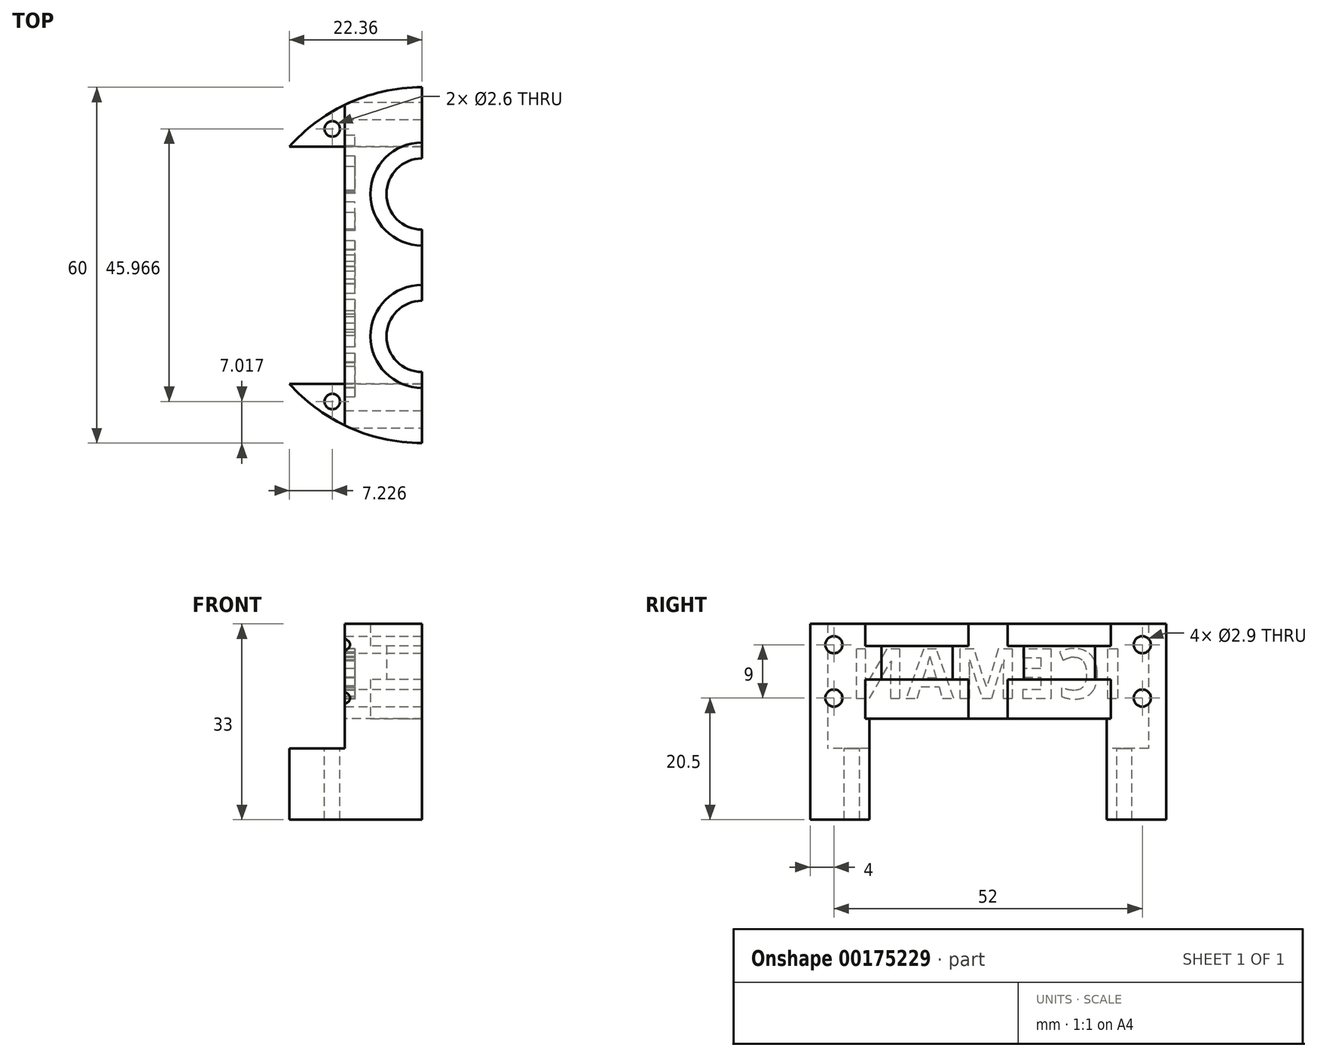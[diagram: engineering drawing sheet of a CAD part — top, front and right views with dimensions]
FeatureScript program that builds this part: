
annotation { "Feature Type Name" : "Feature", "Feature Type Description" : "" }
export const myFeature = defineFeature(function(context is Context, id is Id, definition is map)
    precondition{}
    {
        {
            var Q0;
            Q0=qCreatedBy(makeId("Top.planeOp"),FACE);
            var sketch = newSketch(context, id + "F0", { "sketchPlane" : qUnion([Q0])});
            skLineSegment(sketch, "E0.bottom", {"start": v(-13, -12) * mm, "end": v(13, -12) * mm});
            skLineSegment(sketch, "E0.top", {"start": v(-13, 12) * mm, "end": v(13, 12) * mm});
            skLineSegment(sketch, "E0.left", {"start": v(-13, -12) * mm, "end": v(-13, 12) * mm});
            skLineSegment(sketch, "E0.right", {"start": v(13, -12) * mm, "end": v(13, 12) * mm});
            skPoint(sketch, "E0.middle", {"position": v(0, 0) * mm});
            skCircle(sketch, "E1", {"center": v(0, 0) * mm, "radius": 20 * mm, "construction": true});
            skLineSegment(sketch, "E2", {"start": v(-31.1, 0) * mm, "end": v(39.02, 0) * mm, "construction": true});
            skCircle(sketch, "E3", {"center": v(0, 0) * mm, "radius": 30 * mm});
            skCircle(sketch, "E4", {"center": v(0, 12) * mm, "radius": 6 * mm});
            skCircle(sketch, "E5", {"center": v(0, -12) * mm, "radius": 6 * mm});
            skLineSegment(sketch, "E6.bottom", {"start": v(-13, 27.04) * mm, "end": v(13, 27.04) * mm});
            skLineSegment(sketch, "E6.top", {"start": v(-13, -27.04) * mm, "end": v(13, -27.04) * mm});
            skLineSegment(sketch, "E6.left", {"start": v(-13, 27.04) * mm, "end": v(-13, -27.04) * mm});
            skLineSegment(sketch, "E6.right", {"start": v(13, 27.04) * mm, "end": v(13, -27.04) * mm});
            skSolve(sketch);
        }
        {
            var Q0;
            {var subQ0=sQuery(id+"F0.wireOp",EDGE,"E6.bottom");Q0=makeQuery(id+"F0.imprint","IMPRINT",FACE,{"disambiguationData":[TD([[makeQuery(id+"F0.imprint","IMPRINT",EDGE,{"derivedFrom":subQ0}),1.0]])]});}
            var Q1;
            {var subQ0=sQuery(id+"F0.wireOp",EDGE,"E6.top");Q1=makeQuery(id+"F0.imprint","IMPRINT",FACE,{"disambiguationData":[TD([[makeQuery(id+"F0.imprint","IMPRINT",EDGE,{"derivedFrom":subQ0}),-1.0]])]});}
            var Q2;
            {var subQ0=sQuery(id+"F0.wireOp",EDGE,"E6.top");Q2=makeQuery(id+"F0.imprint","IMPRINT",FACE,{"disambiguationData":[TD([[makeQuery(id+"F0.imprint","IMPRINT",EDGE,{"derivedFrom":subQ0}),1.0]])]});}
            var Q3;
            {var subQ6=sQuery(id+"F0.wireOp",EDGE,"E0.bottom");var subQ9=sQuery(id+"F0.wireOp",EDGE,"E6.left");var subQ13=makeQuery(id+"F0.imprint","INTERSECT",VERTEX,{"derivedFrom":[subQ6,subQ9]});Q3=makeQuery(id+"F0.imprint","IMPRINT",FACE,{"disambiguationData":[TD([[makeQuery(id+"F0.imprint","IMPRINT",EDGE,{"disambiguationData":[TD([[subQ13,-1.0]])],"derivedFrom":subQ6}),1.0]])]});}
            var Q4;
            {var subQ0=sQuery(id+"F0.wireOp",EDGE,"E6.bottom");Q4=makeQuery(id+"F0.imprint","IMPRINT",FACE,{"disambiguationData":[TD([[makeQuery(id+"F0.imprint","IMPRINT",EDGE,{"derivedFrom":subQ0}),-1.0]])]});}
            extrude(context, id + "F1", {"entities" : qUnion([Q0, Q1, Q2, Q3, Q4]), "depth" : 33 * mm});
        }
        {
            var Q0;
            Q0=qCreatedBy(makeId("Top.planeOp"),FACE);
            var sketch = newSketch(context, id + "F2", { "sketchPlane" : qUnion([Q0])});
            skCircle(sketch, "E7", {"center": v(0, 0) * mm, "radius": 30 * mm});
            skCircle(sketch, "E8", {"center": v(-26.68, -13.72) * mm, "radius": 7.63 * mm});
            skLineSegment(sketch, "E9", {"start": v(-22.36, -20) * mm, "end": v(-12.88, -20) * mm});
            skLineSegment(sketch, "E10", {"start": v(-12.88, -20) * mm, "end": v(22.36, -20) * mm});
            skLineSegment(sketch, "E11", {"start": v(22.36, -20) * mm, "end": v(-53.5, 0) * mm, "construction": true});
            skLineSegment(sketch, "E12", {"start": v(-53.5, 0) * mm, "end": v(57.64, 0) * mm, "construction": true});
            skLineSegment(sketch, "E13.MirrorCS", {"start": v(-12.88, 20) * mm, "end": v(22.36, 20) * mm});
            skLineSegment(sketch, "E14.MirrorCS", {"start": v(-22.36, 20) * mm, "end": v(-12.88, 20) * mm});
            skSolve(sketch);
        }
        {
            var Q0;
            {var subQ0=sQuery(id+"F2.wireOp",EDGE,"E13.MirrorCS");Q0=makeQuery(id+"F2.imprint","IMPRINT",FACE,{"disambiguationData":[TD([[makeQuery(id+"F2.imprint","IMPRINT",EDGE,{"derivedFrom":subQ0}),1.0]])]});}
            var Q1;
            {var subQ0=sQuery(id+"F2.wireOp",EDGE,"E9");Q1=makeQuery(id+"F2.imprint","IMPRINT",FACE,{"disambiguationData":[TD([[makeQuery(id+"F2.imprint","IMPRINT",EDGE,{"derivedFrom":subQ0}),-1.0]])]});}
            extrude(context, id + "F3", {"entities" : qUnion([Q0, Q1]), "operationType" : NewBodyOperationType.ADD, "depth" : 12 * mm});
        }
        {
            var Q0;
            Q0=makeQuery(id+"F1.opExtrude","CAP_FACE",FACE,{"disambiguationData":[OSD([sQuery(id+"F0.wireOp",EDGE,"E3"),sQuery(id+"F0.wireOp",EDGE,"E4"),sQuery(id+"F0.wireOp",EDGE,"E5"),sQuery(id+"F0.wireOp",EDGE,"E6.left"),sQuery(id+"F0.wireOp",EDGE,"E6.right")])],"isStart":false});
            var sketch = newSketch(context, id + "F4", { "sketchPlane" : qUnion([Q0])});
            skLineSegment(sketch, "E15", {"start": v(0, 35.89) * mm, "end": v(0, -37.95) * mm});
            skPoint(sketch, "E15.endSnap0", {"position": v(0, 30) * mm});
            skLineSegment(sketch, "E16", {"start": v(0, -37.95) * mm, "end": v(28.6, -37.95) * mm});
            skLineSegment(sketch, "E17", {"start": v(28.6, -37.95) * mm, "end": v(28.6, 36.6) * mm});
            skLineSegment(sketch, "E18", {"start": v(28.6, 36.6) * mm, "end": v(0, 36.6) * mm});
            skLineSegment(sketch, "E19", {"start": v(0, 36.6) * mm, "end": v(0, 33.04) * mm});
            skSolve(sketch);
        }
        {
            var Q0;
            Q0=makeQuery(id+"F1.opExtrude","SWEPT_FACE",FACE,{"disambiguationData":[OSD([sQuery(id+"F0.wireOp",EDGE,"E6.left")])]});
            var sketch = newSketch(context, id + "F5", { "sketchPlane" : qUnion([Q0])});
            skLineSegment(sketch, "E20.bottom", {"start": v(-20, 0) * mm, "end": v(20, 0) * mm});
            skLineSegment(sketch, "E20.top", {"start": v(-20, 17) * mm, "end": v(20, 17) * mm});
            skLineSegment(sketch, "E20.left", {"start": v(-20, 0) * mm, "end": v(-20, 17) * mm});
            skLineSegment(sketch, "E20.right", {"start": v(20, 0) * mm, "end": v(20, 17) * mm});
            skSolve(sketch);
        }
        {
            var Q0;
            {var subQ5=sQuery(id+"F5.wireOp",EDGE,"E20.bottom");Q0=makeQuery(id+"F5.imprint","IMPRINT",FACE,{"disambiguationData":[TD([[makeQuery(id+"F5.imprint","IMPRINT",EDGE,{"derivedFrom":subQ5}),1.0]])]});}
            extrude(context, id + "F6", {"entities" : qUnion([Q0]), "operationType" : NewBodyOperationType.REMOVE, "endBound" : BoundingType.THROUGH_ALL, "oppositeDirection" : true, "depth" : 25 * mm});
        }
        {
            var Q0;
            Q0=makeQuery(id+"F6.boolean.opBoolean","COPY",FACE,{"derivedFrom":makeQuery(id+"F6.opExtrude","SWEPT_FACE",FACE,{"disambiguationData":[OSD([sQuery(id+"F5.wireOp",EDGE,"E20.top")])]})});
            var sketch = newSketch(context, id + "F7", { "sketchPlane" : qUnion([Q0])});
            skCircle(sketch, "E21", {"center": v(0, 12) * mm, "radius": 11.29 * mm, "construction": true});
            skCircle(sketch, "E22", {"center": v(0, -12) * mm, "radius": 11.29 * mm, "construction": true});
            skCircle(sketch, "E23", {"center": v(0, 12) * mm, "radius": 11.29 * mm});
            skCircle(sketch, "E24", {"center": v(0, -12) * mm, "radius": 11.29 * mm});
            skSolve(sketch);
        }
        {
            var Q0;
            Q0=makeQuery(id+"F7.imprint","IMPRINT",FACE,{"disambiguationData":[TD([[makeQuery(id+"F7.imprint","IMPRINT",EDGE,{"derivedFrom":makeQuery(id+"F6.boolean.opBoolean","INTERSECT",EDGE,{"derivedFrom":[makeQuery(id+"F1.opExtrude","SWEPT_FACE",FACE,{"disambiguationData":[OSD([sQuery(id+"F0.wireOp",EDGE,"E4")])]}),makeQuery(id+"F6.opExtrude","SWEPT_FACE",FACE,{"disambiguationData":[OSD([sQuery(id+"F5.wireOp",EDGE,"E20.top")])]})]})}),1.0]])]});
            var Q1;
            Q1=makeQuery(id+"F7.imprint","IMPRINT",FACE,{"disambiguationData":[TD([[makeQuery(id+"F7.imprint","IMPRINT",EDGE,{"derivedFrom":makeQuery(id+"F6.boolean.opBoolean","INTERSECT",EDGE,{"derivedFrom":[makeQuery(id+"F1.opExtrude","SWEPT_FACE",FACE,{"disambiguationData":[OSD([sQuery(id+"F0.wireOp",EDGE,"E5")])]}),makeQuery(id+"F6.opExtrude","SWEPT_FACE",FACE,{"disambiguationData":[OSD([sQuery(id+"F5.wireOp",EDGE,"E20.top")])]})]})}),1.0]])]});
            var Q2;
            {var subQ0=sQuery(id+"F7.wireOp",EDGE,"E23");var subQ1=makeQuery(id+"F6.boolean.opBoolean","COPY",EDGE,{"derivedFrom":makeQuery(id+"F6.opExtrude","SWEPT_EDGE",EDGE,{"disambiguationData":[OSD([sQuery(id+"F5.wireOp",EDGE,"E20.top"),sQuery(id+"F5.wireOp",EDGE,"E20.right")])]})});var subQ2=makeQuery(id+"F7.imprint","INTERSECT",VERTEX,{"disambiguationData":[OD(0.0)],"derivedFrom":[subQ1,subQ0]});Q2=makeQuery(id+"F7.imprint","IMPRINT",FACE,{"disambiguationData":[TD([[makeQuery(id+"F7.imprint","IMPRINT",EDGE,{"disambiguationData":[TD([[subQ2,1.0]])],"derivedFrom":subQ0}),1.0]])]});}
            var Q3;
            {var subQ0=sQuery(id+"F7.wireOp",EDGE,"E24");var subQ1=makeQuery(id+"F6.boolean.opBoolean","COPY",EDGE,{"derivedFrom":makeQuery(id+"F6.opExtrude","SWEPT_EDGE",EDGE,{"disambiguationData":[OSD([sQuery(id+"F5.wireOp",EDGE,"E20.top"),sQuery(id+"F5.wireOp",EDGE,"E20.left")])]})});var subQ2=makeQuery(id+"F7.imprint","INTERSECT",VERTEX,{"disambiguationData":[OD(0.0)],"derivedFrom":[subQ1,subQ0]});Q3=makeQuery(id+"F7.imprint","IMPRINT",FACE,{"disambiguationData":[TD([[makeQuery(id+"F7.imprint","IMPRINT",EDGE,{"disambiguationData":[TD([[subQ2,-1.0]])],"derivedFrom":subQ0}),1.0]])]});}
            var Q4;
            {var subQ1=sQuery(id+"F5.wireOp",EDGE,"E20.top");Q4=makeQuery(id+"F7.imprint","IMPRINT",FACE,{"disambiguationData":[TD([[makeQuery(id+"F7.imprint","IMPRINT",EDGE,{"derivedFrom":makeQuery(id+"F6.boolean.opBoolean","INTERSECT",EDGE,{"derivedFrom":[makeQuery(id+"F1.opExtrude","SWEPT_FACE",FACE,{"disambiguationData":[OSD([sQuery(id+"F0.wireOp",EDGE,"E5")])]}),makeQuery(id+"F6.opExtrude","SWEPT_FACE",FACE,{"disambiguationData":[OSD([subQ1])]})]})}),-1.0]])]});}
            extrude(context, id + "F8", {"entities" : qUnion([Q0, Q1, Q2, Q3, Q4]), "operationType" : NewBodyOperationType.REMOVE, "endBound" : BoundingType.THROUGH_ALL, "depth" : 25 * mm});
        }
        {
            var Q0;
            {var subQ0=sQuery(id+"F0.wireOp",EDGE,"E6.right");var subQ1=makeQuery(id+"F1.opExtrude","CAP_EDGE",EDGE,{"disambiguationData":[OSD([subQ0])],"isStart":false});Q0=makeQuery(id+"F4.imprint","IMPRINT",FACE,{"disambiguationData":[TD([[makeQuery(id+"F4.imprint","IMPRINT",EDGE,{"derivedFrom":subQ1}),-1.0]])]});}
            var sketch = newSketch(context, id + "F9", { "sketchPlane" : qUnion([Q0])});
            skLineSegment(sketch, "E25.bottom", {"start": v(13, 20) * mm, "end": v(-13, 20) * mm});
            skLineSegment(sketch, "E25.top", {"start": v(13, -20) * mm, "end": v(-13, -20) * mm});
            skLineSegment(sketch, "E25.left", {"start": v(13, 20) * mm, "end": v(13, -20) * mm});
            skLineSegment(sketch, "E25.right", {"start": v(-13, 20) * mm, "end": v(-13, -20) * mm});
            skPoint(sketch, "E25.middle", {"position": v(0, 0) * mm});
            skLineSegment(sketch, "E26.bottom", {"start": v(8.83, 20) * mm, "end": v(17.17, 20) * mm});
            skLineSegment(sketch, "E26.top", {"start": v(8.83, -20) * mm, "end": v(17.17, -20) * mm});
            skLineSegment(sketch, "E26.left", {"start": v(8.83, 20) * mm, "end": v(8.83, -20) * mm});
            skLineSegment(sketch, "E26.right", {"start": v(17.17, 20) * mm, "end": v(17.17, -20) * mm});
            skPoint(sketch, "E26.middle", {"position": v(13, 0) * mm});
            skSolve(sketch);
        }
        {
            var Q0;
            {var subQ0=sQuery(id+"F9.wireOp",EDGE,"E26.left");Q0=makeQuery(id+"F9.imprint","IMPRINT",FACE,{"disambiguationData":[TD([[makeQuery(id+"F9.imprint","IMPRINT",EDGE,{"derivedFrom":subQ0}),1.0]])]});}
            extrude(context, id + "F10", {"entities" : qUnion([Q0]), "operationType" : NewBodyOperationType.ADD, "depth" : 8 * mm});
        }
        {
            var Q0;
            {var subQ0=sQuery(id+"F0.wireOp",EDGE,"E6.right");Q0=makeQuery(id+"F10.boolean.opBoolean","MERGE",FACE,{"derivedFrom":[makeQuery(id+"F1.opExtrude","SWEPT_FACE",FACE,{"disambiguationData":[OSD([subQ0])]}),makeQuery(id+"F10.opExtrude","SWEPT_FACE",FACE,{"disambiguationData":[OSD([subQ0])]})]});}
            var sketch = newSketch(context, id + "F11", { "sketchPlane" : qUnion([Q0])});
            skLineSegment(sketch, "E27.bottom", {"start": v(-20, 41) * mm, "end": v(20, 41) * mm});
            skLineSegment(sketch, "E27.top", {"start": v(-20, 0) * mm, "end": v(20, 0) * mm});
            skLineSegment(sketch, "E27.left", {"start": v(-20, 41) * mm, "end": v(-20, 0) * mm});
            skLineSegment(sketch, "E27.right", {"start": v(20, 41) * mm, "end": v(20, 0) * mm});
            skLineSegment(sketch, "E28", {"start": v(-20, 36) * mm, "end": v(20, 36) * mm, "construction": true});
            skCircle(sketch, "E29", {"center": v(-16, 36) * mm, "radius": 1.4 * mm});
            skCircle(sketch, "E30", {"center": v(16, 36) * mm, "radius": 1.4 * mm});
            skSolve(sketch);
        }
        {
            var Q0;
            Q0=makeQuery(id+"F11.imprint","IMPRINT",FACE,{"disambiguationData":[TD([[makeQuery(id+"F11.imprint","IMPRINT",EDGE,{"derivedFrom":sQuery(id+"F11.wireOp",EDGE,"E29")}),1.0]])]});
            var Q1;
            Q1=makeQuery(id+"F11.imprint","IMPRINT",FACE,{"disambiguationData":[TD([[makeQuery(id+"F11.imprint","IMPRINT",EDGE,{"derivedFrom":sQuery(id+"F11.wireOp",EDGE,"E30")}),1.0]])]});
            extrude(context, id + "F12", {"entities" : qUnion([Q0, Q1]), "operationType" : NewBodyOperationType.REMOVE, "endBound" : BoundingType.THROUGH_ALL, "oppositeDirection" : true, "depth" : 25 * mm});
        }
        {
            var Q0;
            {var subQ0=sQuery(id+"F0.wireOp",EDGE,"E6.left");var subQ1=makeQuery(id+"F1.opExtrude","CAP_EDGE",EDGE,{"disambiguationData":[OSD([subQ0])],"isStart":false});Q0=makeQuery(id+"F4.imprint","IMPRINT",FACE,{"disambiguationData":[TD([[makeQuery(id+"F4.imprint","IMPRINT",EDGE,{"derivedFrom":subQ1}),1.0]])]});}
            var sketch = newSketch(context, id + "F13", { "sketchPlane" : qUnion([Q0])});
            skLineSegment(sketch, "E31", {"start": v(0, 33.3) * mm, "end": v(0, -31.46) * mm});
            skLineSegment(sketch, "E32", {"start": v(0, -31.46) * mm, "end": v(26.28, -31.46) * mm});
            skLineSegment(sketch, "E33", {"start": v(26.28, -31.46) * mm, "end": v(26.28, 32.75) * mm});
            skLineSegment(sketch, "E34", {"start": v(26.28, 32.75) * mm, "end": v(0, 32.75) * mm});
            skSolve(sketch);
        }
        {
            var Q0;
            {var subQ0=sQuery(id+"F4.wireOp",EDGE,"E16");Q0=makeQuery(id+"F4.imprint","IMPRINT",FACE,{"disambiguationData":[TD([[makeQuery(id+"F4.imprint","IMPRINT",EDGE,{"derivedFrom":subQ0}),1.0]])]});}
            var Q1;
            {var subQ0=sQuery(id+"F0.wireOp",EDGE,"E6.right");var subQ1=makeQuery(id+"F1.opExtrude","CAP_EDGE",EDGE,{"disambiguationData":[OSD([subQ0])],"isStart":false});Q1=makeQuery(id+"F4.imprint","IMPRINT",FACE,{"disambiguationData":[TD([[makeQuery(id+"F4.imprint","IMPRINT",EDGE,{"derivedFrom":subQ1}),-1.0]])]});}
            var Q2;
            Q2=makeQuery(id+"F10.opExtrude","CAP_FACE",FACE,{"disambiguationData":[OSD([sQuery(id+"F0.wireOp",EDGE,"E6.right"),sQuery(id+"F9.wireOp",EDGE,"E26.bottom"),sQuery(id+"F9.wireOp",EDGE,"E26.top"),sQuery(id+"F9.wireOp",EDGE,"E26.left")])],"isStart":false});
            extrude(context, id + "F14", {"entities" : qUnion([Q0, Q1, Q2]), "operationType" : NewBodyOperationType.REMOVE, "endBound" : BoundingType.THROUGH_ALL, "oppositeDirection" : true, "depth" : 25 * mm});
        }
        {
            var Q0;
            {var subQ0=sQuery(id+"F4.wireOp",EDGE,"E15");Q0=makeQuery(id+"F14.boolean.opBoolean","COPY",FACE,{"derivedFrom":makeQuery(id+"F14.opExtrude","SWEPT_FACE",FACE,{"disambiguationData":[OSD([subQ0]),TDD([makeQuery(id+"F4.imprint","IMPRINT",EDGE,{"disambiguationData":[TD([[makeQuery(id+"F4.imprint","INTERSECT",VERTEX,{"disambiguationData":[OD(1.0)],"derivedFrom":[makeQuery(id+"F1.opExtrude","CAP_EDGE",EDGE,{"disambiguationData":[OSD([sQuery(id+"F0.wireOp",EDGE,"E4")])],"isStart":false}),subQ0]}),-1.0]])],"derivedFrom":subQ0})])]})});}
            var sketch = newSketch(context, id + "F15", { "sketchPlane" : qUnion([Q0])});
            skLineSegment(sketch, "E35.bottom", {"start": v(0, 33) * mm, "end": v(-6, 33) * mm});
            skLineSegment(sketch, "E35.top", {"start": v(0, 17) * mm, "end": v(-6, 17) * mm});
            skLineSegment(sketch, "E35.left", {"start": v(0, 33) * mm, "end": v(0, 17) * mm});
            skLineSegment(sketch, "E35.right", {"start": v(-6, 33) * mm, "end": v(-6, 17) * mm});
            skLineSegment(sketch, "E36.bottom", {"start": v(6, 25) * mm, "end": v(-6, 25) * mm});
            skLineSegment(sketch, "E36.top", {"start": v(6, 41) * mm, "end": v(-6, 41) * mm});
            skLineSegment(sketch, "E36.left", {"start": v(6, 25) * mm, "end": v(6, 41) * mm});
            skLineSegment(sketch, "E36.right", {"start": v(-6, 25) * mm, "end": v(-6, 41) * mm});
            skPoint(sketch, "E36.middle", {"position": v(0, 33) * mm});
            skLineSegment(sketch, "E37.bottom", {"start": v(-6, 17) * mm, "end": v(18, 17) * mm});
            skLineSegment(sketch, "E37.top", {"start": v(-6, 33) * mm, "end": v(18, 33) * mm});
            skLineSegment(sketch, "E37.left", {"start": v(-6, 17) * mm, "end": v(-6, 33) * mm});
            skLineSegment(sketch, "E37.right", {"start": v(18, 17) * mm, "end": v(18, 33) * mm});
            skPoint(sketch, "E37.middle", {"position": v(6, 25) * mm});
            skLineSegment(sketch, "E38", {"start": v(6, 17) * mm, "end": v(6, 25) * mm});
            skLineSegment(sketch, "E39", {"start": v(18, 25) * mm, "end": v(6, 25) * mm});
            skLineSegment(sketch, "E40", {"start": v(12, 25) * mm, "end": v(12, 33) * mm});
            skLineSegment(sketch, "E41", {"start": v(12, 33) * mm, "end": v(12, 15.18) * mm});
            skLineSegment(sketch, "E42.bottom", {"start": v(12, 33) * mm, "end": v(20.69, 33) * mm});
            skLineSegment(sketch, "E42.top", {"start": v(12, 29.31) * mm, "end": v(20.7, 29.31) * mm});
            skLineSegment(sketch, "E42.left", {"start": v(12, 33) * mm, "end": v(12, 29.31) * mm});
            skLineSegment(sketch, "E42.right", {"start": v(20.69, 33) * mm, "end": v(20.69, 29.31) * mm});
            skLineSegment(sketch, "E43.bottom", {"start": v(12, 23.6) * mm, "end": v(20.69, 23.6) * mm});
            skLineSegment(sketch, "E43.top", {"start": v(12, 17) * mm, "end": v(20.69, 17) * mm});
            skLineSegment(sketch, "E43.left", {"start": v(12, 23.6) * mm, "end": v(12, 17) * mm});
            skLineSegment(sketch, "E43.right", {"start": v(20.69, 23.6) * mm, "end": v(20.69, 17) * mm});
            skSolve(sketch);
        }
        {
            var Q0;
            {var subQ5=sQuery(id+"F15.wireOp",EDGE,"E42.right");Q0=makeQuery(id+"F15.imprint","IMPRINT",FACE,{"disambiguationData":[TD([[makeQuery(id+"F15.imprint","IMPRINT",EDGE,{"derivedFrom":subQ5}),-1.0]])]});}
            var Q1;
            {var subQ5=sQuery(id+"F15.wireOp",EDGE,"E43.right");Q1=makeQuery(id+"F15.imprint","IMPRINT",FACE,{"disambiguationData":[TD([[makeQuery(id+"F15.imprint","IMPRINT",EDGE,{"derivedFrom":subQ5}),-1.0]])]});}
            var Q2;
            Q2=sQuery(id+"F15.wireOp",EDGE,"E41");
            revolve(context, id + "F16", {"operationType" : NewBodyOperationType.REMOVE, "entities" : qUnion([Q0, Q1]), "axis" : qUnion([Q2]), "revolveType" : RevolveType.FULL, "oppositeDirection" : true});
        }
        {
            var Q0;
            {var subQ0=sQuery(id+"F4.wireOp",EDGE,"E15");Q0=makeQuery(id+"F14.boolean.opBoolean","COPY",FACE,{"derivedFrom":makeQuery(id+"F14.opExtrude","SWEPT_FACE",FACE,{"disambiguationData":[OSD([subQ0]),TDD([makeQuery(id+"F4.imprint","IMPRINT",EDGE,{"disambiguationData":[TD([[makeQuery(id+"F4.imprint","INTERSECT",VERTEX,{"disambiguationData":[OD(1.0)],"derivedFrom":[makeQuery(id+"F1.opExtrude","CAP_EDGE",EDGE,{"disambiguationData":[OSD([sQuery(id+"F0.wireOp",EDGE,"E4")])],"isStart":false}),subQ0]}),-1.0]])],"derivedFrom":subQ0})])]})});}
            var sketch = newSketch(context, id + "F17", { "sketchPlane" : qUnion([Q0])});
            skLineSegment(sketch, "E44.bottom", {"start": v(-6, 17) * mm, "end": v(18, 17) * mm});
            skLineSegment(sketch, "E44.top", {"start": v(-6, 41.62) * mm, "end": v(18, 41.62) * mm});
            skLineSegment(sketch, "E44.left", {"start": v(-6, 17) * mm, "end": v(-6, 41.62) * mm});
            skLineSegment(sketch, "E44.right", {"start": v(18, 17) * mm, "end": v(18, 41.62) * mm});
            skPoint(sketch, "E44.middle", {"position": v(6, 29.31) * mm});
            skLineSegment(sketch, "E45.bottom", {"start": v(6, 29.31) * mm, "end": v(-18, 29.31) * mm});
            skLineSegment(sketch, "E45.top", {"start": v(6, 4.69) * mm, "end": v(-18, 4.69) * mm});
            skLineSegment(sketch, "E45.left", {"start": v(6, 29.31) * mm, "end": v(6, 4.69) * mm});
            skLineSegment(sketch, "E45.right", {"start": v(-18, 29.31) * mm, "end": v(-18, 4.69) * mm});
            skPoint(sketch, "E45.middle", {"position": v(-6, 17) * mm});
            skLineSegment(sketch, "E46.bottom", {"start": v(-6, 33) * mm, "end": v(-18, 33) * mm});
            skLineSegment(sketch, "E46.top", {"start": v(-6, 17) * mm, "end": v(-18, 17) * mm});
            skLineSegment(sketch, "E46.left", {"start": v(-6, 33) * mm, "end": v(-6, 17) * mm});
            skLineSegment(sketch, "E46.right", {"start": v(-18, 33) * mm, "end": v(-18, 17) * mm});
            skLineSegment(sketch, "E47.bottom", {"start": v(-3.3, 29.31) * mm, "end": v(-12, 29.31) * mm});
            skLineSegment(sketch, "E47.top", {"start": v(-3.3, 33) * mm, "end": v(-12, 33) * mm});
            skLineSegment(sketch, "E47.left", {"start": v(-3.3, 29.31) * mm, "end": v(-3.3, 33) * mm});
            skLineSegment(sketch, "E47.right", {"start": v(-12, 29.31) * mm, "end": v(-12, 33) * mm});
            skLineSegment(sketch, "E48.bottom", {"start": v(-3.3, 23.6) * mm, "end": v(-12, 23.6) * mm});
            skLineSegment(sketch, "E48.top", {"start": v(-3.3, 17) * mm, "end": v(-12, 17) * mm});
            skLineSegment(sketch, "E48.left", {"start": v(-3.3, 23.6) * mm, "end": v(-3.3, 17) * mm});
            skLineSegment(sketch, "E48.right", {"start": v(-12, 23.6) * mm, "end": v(-12, 17) * mm});
            skSolve(sketch);
        }
        {
            var Q0;
            {var subQ5=sQuery(id+"F17.wireOp",EDGE,"E48.left");Q0=makeQuery(id+"F17.imprint","IMPRINT",FACE,{"disambiguationData":[TD([[makeQuery(id+"F17.imprint","IMPRINT",EDGE,{"derivedFrom":subQ5}),-1.0]])]});}
            var Q1;
            {var subQ5=sQuery(id+"F17.wireOp",EDGE,"E47.left");Q1=makeQuery(id+"F17.imprint","IMPRINT",FACE,{"disambiguationData":[TD([[makeQuery(id+"F17.imprint","IMPRINT",EDGE,{"derivedFrom":subQ5}),1.0]])]});}
            var Q2;
            Q2=sQuery(id+"F17.wireOp",EDGE,"E48.right");
            revolve(context, id + "F18", {"operationType" : NewBodyOperationType.REMOVE, "entities" : qUnion([Q0, Q1]), "axis" : qUnion([Q2]), "revolveType" : RevolveType.FULL, "oppositeDirection" : true});
        }
        {
            var Q0;
            {var subQ0=sQuery(id+"F0.wireOp",EDGE,"E6.left");var subQ1=makeQuery(id+"F1.opExtrude","CAP_EDGE",EDGE,{"disambiguationData":[OSD([subQ0])],"isStart":false});Q0=makeQuery(id+"F13.imprint","IMPRINT",FACE,{"disambiguationData":[TD([[makeQuery(id+"F13.imprint","IMPRINT",EDGE,{"derivedFrom":makeQuery(id+"F4.imprint","IMPRINT",EDGE,{"derivedFrom":subQ1})}),1.0]])]});}
            var sketch = newSketch(context, id + "F19", { "sketchPlane" : qUnion([Q0])});
            skLineSegment(sketch, "E49.bottom", {"start": v(-29.2, -19.64) * mm, "end": v(29.2, -19.64) * mm});
            skLineSegment(sketch, "E49.top", {"start": v(-29.2, 19.64) * mm, "end": v(29.2, 19.64) * mm});
            skLineSegment(sketch, "E49.left", {"start": v(-29.2, -19.64) * mm, "end": v(-29.2, 19.64) * mm});
            skLineSegment(sketch, "E49.right", {"start": v(29.2, -19.64) * mm, "end": v(29.2, 19.64) * mm});
            skPoint(sketch, "E49.middle", {"position": v(0, 0) * mm});
            skLineSegment(sketch, "E50.bottom", {"start": v(-15.13, 22.98) * mm, "end": v(-10.53, 22.98) * mm});
            skLineSegment(sketch, "E50.top", {"start": v(-15.13, -22.98) * mm, "end": v(-10.53, -22.98) * mm});
            skLineSegment(sketch, "E50.left", {"start": v(-15.13, 22.98) * mm, "end": v(-15.13, -22.98) * mm});
            skLineSegment(sketch, "E50.right", {"start": v(-10.53, 22.98) * mm, "end": v(-10.53, -22.98) * mm});
            skPoint(sketch, "E50.middle", {"position": v(-12.83, 0) * mm});
            skCircle(sketch, "E51", {"center": v(-15.13, 22.98) * mm, "radius": 1.3 * mm});
            skCircle(sketch, "E52", {"center": v(-15.13, -22.98) * mm, "radius": 1.3 * mm});
            skSolve(sketch);
        }
        {
            var Q0;
            {var subQ0=sQuery(id+"F19.wireOp",EDGE,"E50.left");var subQ1=sQuery(id+"F19.wireOp",EDGE,"E50.bottom");var subQ2=makeQuery(id+"F19.imprint","INTERSECT",VERTEX,{"derivedFrom":[subQ1,subQ0]});Q0=makeQuery(id+"F19.imprint","IMPRINT",FACE,{"disambiguationData":[TD([[makeQuery(id+"F19.imprint","IMPRINT",EDGE,{"disambiguationData":[TD([[subQ2,-1.0]])],"derivedFrom":subQ1}),1.0]])]});}
            var Q1;
            {var subQ0=sQuery(id+"F19.wireOp",EDGE,"E50.left");var subQ1=sQuery(id+"F19.wireOp",EDGE,"E50.bottom");var subQ2=makeQuery(id+"F19.imprint","INTERSECT",VERTEX,{"derivedFrom":[subQ1,subQ0]});Q1=makeQuery(id+"F19.imprint","IMPRINT",FACE,{"disambiguationData":[TD([[makeQuery(id+"F19.imprint","IMPRINT",EDGE,{"disambiguationData":[TD([[subQ2,-1.0]])],"derivedFrom":subQ1}),-1.0]])]});}
            var Q2;
            {var subQ0=sQuery(id+"F19.wireOp",EDGE,"E50.left");var subQ1=sQuery(id+"F19.wireOp",EDGE,"E50.top");var subQ2=makeQuery(id+"F19.imprint","INTERSECT",VERTEX,{"derivedFrom":[subQ1,subQ0]});Q2=makeQuery(id+"F19.imprint","IMPRINT",FACE,{"disambiguationData":[TD([[makeQuery(id+"F19.imprint","IMPRINT",EDGE,{"disambiguationData":[TD([[subQ2,-1.0]])],"derivedFrom":subQ1}),-1.0]])]});}
            var Q3;
            {var subQ0=sQuery(id+"F19.wireOp",EDGE,"E50.left");var subQ1=sQuery(id+"F19.wireOp",EDGE,"E50.top");var subQ2=makeQuery(id+"F19.imprint","INTERSECT",VERTEX,{"derivedFrom":[subQ1,subQ0]});Q3=makeQuery(id+"F19.imprint","IMPRINT",FACE,{"disambiguationData":[TD([[makeQuery(id+"F19.imprint","IMPRINT",EDGE,{"disambiguationData":[TD([[subQ2,-1.0]])],"derivedFrom":subQ1}),1.0]])]});}
            extrude(context, id + "F20", {"entities" : qUnion([Q0, Q1, Q2, Q3]), "operationType" : NewBodyOperationType.REMOVE, "endBound" : BoundingType.THROUGH_ALL, "oppositeDirection" : true, "depth" : 25 * mm});
        }
        {
            var Q0;
            Q0=makeQuery(id+"F1.opExtrude","SWEPT_FACE",FACE,{"disambiguationData":[OSD([sQuery(id+"F0.wireOp",EDGE,"E6.left")])]});
            var sketch = newSketch(context, id + "F21", { "sketchPlane" : qUnion([Q0])});
            skText(sketch, "E53", { "text": "ICEMAN\n", "fontName": "OpenSans-Bold.ttf"});
            skPoint(sketch, "E54", {"position": v(0, 33) * mm});
            const initialGuessF21  = {"E53": [-0.02293, 0.02045, 1, 0, 0.00837]};
            skSetInitialGuess(sketch, initialGuessF21);
            skSolve(sketch);
        }
        {
            var Q0;
            Q0 = qSketchRegion(id + "F21", true);
            extrude(context, id + "F22", {"entities" : qUnion([Q0]), "operationType" : NewBodyOperationType.REMOVE, "oppositeDirection" : true, "depth" : 1.69 * mm});
        }
        {
            var Q0;
            {var subQ0=sQuery(id+"F4.wireOp",EDGE,"E15");Q0=makeQuery(id+"F14.boolean.opBoolean","COPY",FACE,{"derivedFrom":makeQuery(id+"F14.opExtrude","SWEPT_FACE",FACE,{"disambiguationData":[OSD([subQ0]),TDD([makeQuery(id+"F4.imprint","IMPRINT",EDGE,{"disambiguationData":[TD([[makeQuery(id+"F4.imprint","INTERSECT",VERTEX,{"disambiguationData":[OD(1.0)],"derivedFrom":[makeQuery(id+"F1.opExtrude","CAP_EDGE",EDGE,{"disambiguationData":[OSD([sQuery(id+"F0.wireOp",EDGE,"E4")])],"isStart":false}),subQ0]}),-1.0]])],"derivedFrom":subQ0})])]})});}
            var sketch = newSketch(context, id + "F23", { "sketchPlane" : qUnion([Q0])});
            skLineSegment(sketch, "E55.bottom", {"start": v(3.3, 17) * mm, "end": v(-3.3, 17) * mm});
            skLineSegment(sketch, "E55.top", {"start": v(3.3, 33) * mm, "end": v(-3.3, 33) * mm});
            skLineSegment(sketch, "E55.left", {"start": v(3.3, 17) * mm, "end": v(3.3, 33) * mm});
            skLineSegment(sketch, "E55.right", {"start": v(-3.3, 17) * mm, "end": v(-3.3, 33) * mm});
            skLineSegment(sketch, "E56.bottom", {"start": v(3.3, 25) * mm, "end": v(-3.3, 25) * mm});
            skLineSegment(sketch, "E56.top", {"start": v(3.3, 20.3) * mm, "end": v(-3.3, 20.3) * mm});
            skLineSegment(sketch, "E56.left", {"start": v(3.3, 25) * mm, "end": v(3.3, 20.3) * mm});
            skLineSegment(sketch, "E56.right", {"start": v(-3.3, 25) * mm, "end": v(-3.3, 20.3) * mm});
            skCircle(sketch, "E57", {"center": v(0, 25) * mm, "radius": 1.4 * mm});
            skLineSegment(sketch, "E58", {"start": v(0, 25) * mm, "end": v(32.02, 25) * mm});
            skLineSegment(sketch, "E59", {"start": v(32.02, 25) * mm, "end": v(-32.68, 25) * mm});
            skLineSegment(sketch, "E60.bottom", {"start": v(26, 20.5) * mm, "end": v(-26, 20.5) * mm});
            skLineSegment(sketch, "E60.top", {"start": v(26, 29.5) * mm, "end": v(-26, 29.5) * mm});
            skLineSegment(sketch, "E60.left", {"start": v(26, 20.5) * mm, "end": v(26, 29.5) * mm});
            skLineSegment(sketch, "E60.right", {"start": v(-26, 20.5) * mm, "end": v(-26, 29.5) * mm});
            skCircle(sketch, "E61", {"center": v(-26, 29.5) * mm, "radius": 1.45 * mm});
            skCircle(sketch, "E62", {"center": v(-26, 20.5) * mm, "radius": 1.45 * mm});
            skCircle(sketch, "E63", {"center": v(26, 29.5) * mm, "radius": 1.45 * mm});
            skCircle(sketch, "E64", {"center": v(26, 20.5) * mm, "radius": 1.45 * mm});
            skSolve(sketch);
        }
        {
            var Q0;
            {var subQ0=sQuery(id+"F23.wireOp",EDGE,"E59");var subQ4=makeQuery(id+"F23.imprint","IMPRINT",VERTEX,{"derivedFrom":subQ0});Q0=makeQuery(id+"F23.imprint","IMPRINT",FACE,{"disambiguationData":[TD([[makeQuery(id+"F23.imprint","IMPRINT",EDGE,{"disambiguationData":[TD([[subQ4,1.0]])],"derivedFrom":subQ0}),-1.0]])]});}
            var Q1;
            {var subQ0=sQuery(id+"F23.wireOp",EDGE,"E59");var subQ4=makeQuery(id+"F23.imprint","IMPRINT",VERTEX,{"derivedFrom":subQ0});Q1=makeQuery(id+"F23.imprint","IMPRINT",FACE,{"disambiguationData":[TD([[makeQuery(id+"F23.imprint","IMPRINT",EDGE,{"disambiguationData":[TD([[subQ4,1.0]])],"derivedFrom":subQ0}),1.0]])]});}
            var Q2;
            {var subQ0=sQuery(id+"F23.wireOp",EDGE,"E60.right");var subQ1=sQuery(id+"F23.wireOp",EDGE,"E60.top");var subQ2=makeQuery(id+"F23.imprint","INTERSECT",VERTEX,{"derivedFrom":[subQ1,subQ0]});Q2=makeQuery(id+"F23.imprint","IMPRINT",FACE,{"disambiguationData":[TD([[makeQuery(id+"F23.imprint","IMPRINT",EDGE,{"disambiguationData":[TD([[subQ2,1.0]])],"derivedFrom":subQ1}),-1.0]])]});}
            var Q3;
            {var subQ0=sQuery(id+"F23.wireOp",EDGE,"E60.right");var subQ1=sQuery(id+"F23.wireOp",EDGE,"E60.top");var subQ2=makeQuery(id+"F23.imprint","INTERSECT",VERTEX,{"derivedFrom":[subQ1,subQ0]});Q3=makeQuery(id+"F23.imprint","IMPRINT",FACE,{"disambiguationData":[TD([[makeQuery(id+"F23.imprint","IMPRINT",EDGE,{"disambiguationData":[TD([[subQ2,1.0]])],"derivedFrom":subQ1}),1.0]])]});}
            var Q4;
            {var subQ0=sQuery(id+"F23.wireOp",EDGE,"E60.right");var subQ1=sQuery(id+"F23.wireOp",EDGE,"E60.bottom");var subQ2=makeQuery(id+"F23.imprint","INTERSECT",VERTEX,{"derivedFrom":[subQ1,subQ0]});Q4=makeQuery(id+"F23.imprint","IMPRINT",FACE,{"disambiguationData":[TD([[makeQuery(id+"F23.imprint","IMPRINT",EDGE,{"disambiguationData":[TD([[subQ2,1.0]])],"derivedFrom":subQ1}),1.0]])]});}
            var Q5;
            {var subQ0=sQuery(id+"F23.wireOp",EDGE,"E60.right");var subQ1=sQuery(id+"F23.wireOp",EDGE,"E60.bottom");var subQ2=makeQuery(id+"F23.imprint","INTERSECT",VERTEX,{"derivedFrom":[subQ1,subQ0]});Q5=makeQuery(id+"F23.imprint","IMPRINT",FACE,{"disambiguationData":[TD([[makeQuery(id+"F23.imprint","IMPRINT",EDGE,{"disambiguationData":[TD([[subQ2,1.0]])],"derivedFrom":subQ1}),-1.0]])]});}
            var Q6;
            {var subQ0=sQuery(id+"F23.wireOp",EDGE,"E60.left");var subQ1=sQuery(id+"F23.wireOp",EDGE,"E60.top");var subQ2=makeQuery(id+"F23.imprint","INTERSECT",VERTEX,{"derivedFrom":[subQ1,subQ0]});Q6=makeQuery(id+"F23.imprint","IMPRINT",FACE,{"disambiguationData":[TD([[makeQuery(id+"F23.imprint","IMPRINT",EDGE,{"disambiguationData":[TD([[subQ2,-1.0]])],"derivedFrom":subQ1}),1.0]])]});}
            var Q7;
            {var subQ0=sQuery(id+"F23.wireOp",EDGE,"E60.left");var subQ1=sQuery(id+"F23.wireOp",EDGE,"E60.top");var subQ2=makeQuery(id+"F23.imprint","INTERSECT",VERTEX,{"derivedFrom":[subQ1,subQ0]});Q7=makeQuery(id+"F23.imprint","IMPRINT",FACE,{"disambiguationData":[TD([[makeQuery(id+"F23.imprint","IMPRINT",EDGE,{"disambiguationData":[TD([[subQ2,-1.0]])],"derivedFrom":subQ1}),-1.0]])]});}
            var Q8;
            {var subQ0=sQuery(id+"F23.wireOp",EDGE,"E60.left");var subQ1=sQuery(id+"F23.wireOp",EDGE,"E60.bottom");var subQ2=makeQuery(id+"F23.imprint","INTERSECT",VERTEX,{"derivedFrom":[subQ1,subQ0]});Q8=makeQuery(id+"F23.imprint","IMPRINT",FACE,{"disambiguationData":[TD([[makeQuery(id+"F23.imprint","IMPRINT",EDGE,{"disambiguationData":[TD([[subQ2,-1.0]])],"derivedFrom":subQ1}),1.0]])]});}
            var Q9;
            {var subQ0=sQuery(id+"F23.wireOp",EDGE,"E60.left");var subQ1=sQuery(id+"F23.wireOp",EDGE,"E60.bottom");var subQ2=makeQuery(id+"F23.imprint","INTERSECT",VERTEX,{"derivedFrom":[subQ1,subQ0]});Q9=makeQuery(id+"F23.imprint","IMPRINT",FACE,{"disambiguationData":[TD([[makeQuery(id+"F23.imprint","IMPRINT",EDGE,{"disambiguationData":[TD([[subQ2,-1.0]])],"derivedFrom":subQ1}),-1.0]])]});}
            extrude(context, id + "F24", {"entities" : qUnion([Q0, Q1, Q2, Q3, Q4, Q5, Q6, Q7, Q8, Q9]), "operationType" : NewBodyOperationType.REMOVE, "endBound" : BoundingType.THROUGH_ALL, "oppositeDirection" : true, "depth" : 25 * mm});
        }
    });
